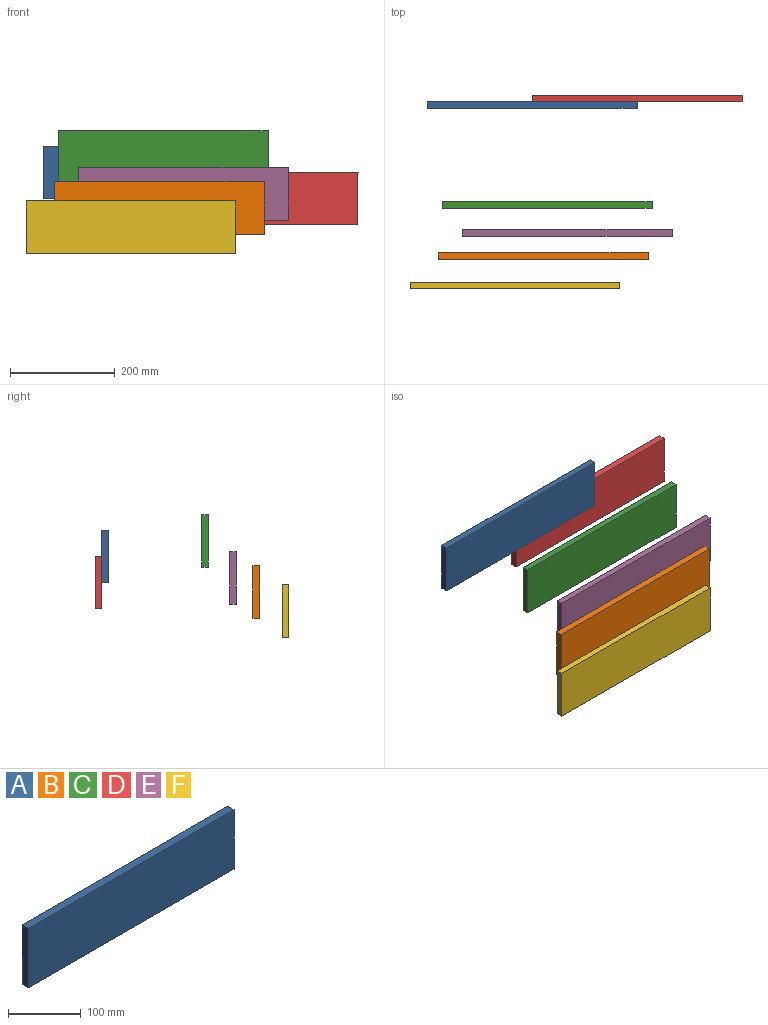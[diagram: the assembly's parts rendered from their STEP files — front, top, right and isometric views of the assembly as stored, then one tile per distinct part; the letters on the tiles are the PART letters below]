
ASSEMBLY  parts=6 mates=1
PART A: 6 faces, bbox 400x12.5x100 mm
  f0: plane 100x12.5mm, normal (-1,0,0), area 1250mm2, adj f1,f3,f4,f5
  f1: plane 400x12.5mm, normal (0,0,-1), area 5000mm2, adj f0,f2,f4,f5
  f2: plane 100x12.5mm, normal (1,0,0), area 1250mm2, adj f1,f3,f4,f5
  f3: plane 400x12.5mm, normal (0,0,1), area 5000mm2, adj f0,f2,f4,f5
  f4: plane 400x100mm, normal (0,-1,0), area 40000mm2, adj f0,f1,f2,f3
  f5: plane 400x100mm, normal (0,1,0), area 40000mm2, adj f0,f1,f2,f3
PART B: same geometry as A
PART C: same geometry as A
PART D: same geometry as A
PART E: same geometry as A
PART F: same geometry as A
PLACE A rot(axis=(0,-1,0),180deg) t=(191.51,176.06,-69.93)mm
PLACE B t=(-187.33,-111.78,-238.02)mm
PLACE C t=(-179.97,-14.14,-140.41)mm
PLACE D t=(-8.49,188.56,-219.93)mm
PLACE E t=(-141.37,-67.34,-211.16)mm
PLACE F t=(-241.24,-167.26,-274.54)mm
MATE parallel A.f5 <-> D.f4  axis (0,1,0) through (191.51,176.06,-169.93)mm
